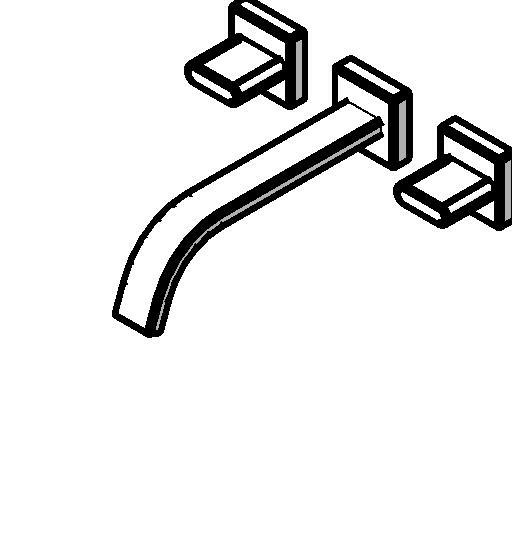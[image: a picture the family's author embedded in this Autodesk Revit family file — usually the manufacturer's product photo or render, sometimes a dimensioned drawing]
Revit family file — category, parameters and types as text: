
# Revit family: Deca_Misturador de parede para lavatório_Polo_1878.33
name_source: partatom
category: Plumbing Fixtures
units: mm (PartAtom-declared; Revit-internal decimal feet)

## family parameters
Cut with Voids When Loaded = No
Host = Face
Part Type = Normal
Room Calculation Point = No
Round Connector Dimension = Use Radius
Shared = No

## types (4) — shared parameters
Acompanha o Produto = Acompanha Deca confort
Aprovado por = quattroD
Atendimento ao Cliente = 0800-0117073
CW Connection = No
Categoria = METAIS PARA BANHEIRO
Composição Anel Vedação = -
Composição Assento = -
Composição Básica = Liga de Cobre (bronze e latão),Plásticos de Engenharia,Elastômeros
Composição Componente = -
Consumo = -
Cor Interna = -
Cor Secundária = -
Cores Componente = -
Criado por = quattroD
Código Pai = 1878.33
Default Elevation = 1100 mm
Description = Misturador de parede para lavatório
Diâmetro Água Fria = 20 mm  [stored 0.0656168 ft]
Diâmetro Água Quente = 20 mm  [stored 0.0656168 ft]
HW Connection = No
Informações Complementares = -
Itens de Instalação = -
Linha = Polo
Manufacturer = Deca
Norma = NBR16749
Pressão máx. funcionamento = 40 MCA
Pressão mín. Aquec. Acúmulo = -
Pressão mín. Aquec. Passagem = -
Pressão mín. funcionamento = 2 MCA
Raio Água Fria = 10 mm  [stored 0.0328084 ft]
Raio Água Quente = 10 mm  [stored 0.0328084 ft]
Saída de Esgoto = -
Segmento = Banheiro Médio
Tipo de dispositivo economizador = Sim
Tipo de mecanismo utilizado = MVC -1/4 volta
Tipo de rosca de entrada = BSP NBR 8133
Tipo de rosca de saída = -
URL = www.deca.com.br
Vazão na Pressão máx. (L/min) = 6
Vazão na Pressão mín. (L/min) = 4
Vent Connection = No
Waste Connection = No
zero-valued in all types: CWFU, HWFU, WFU

## per-type parameters (varying)
| type | Cor Principal | Material | Model | Peso Líquido (Kg) |
| 1878.C33_Cromado | Cromado | Deca_Cromado | 1878.C33 | 2.491 |
| 1878.BL33.NO_Black Noir | Black Noir | Deca_Black Noir | 1878.BL33.NO | 2.491 |
| 1878.GL33_Gold | Gold | Deca_Gold | 1878.GL33 | 2.399 |
| 1878.GL33.RD_Red Gold | Red Gold | Deca_Red Gold | 1878.GL33.RD | 2.491 |

note: source unit labels omitted for Vazão na Pressão máx. (L/min), Vazão na Pressão mín. (L/min) — the stored unit's dimension contradicts the parameter name (converter mislabeling)

note: [stored X ft] marks values corroborated as IEEE doubles in the binary element streams (Revit-internal decimal feet)

## geometry (parser evidence)
native form markers: Sweep x2
no freeform markers — native parametric forms only
